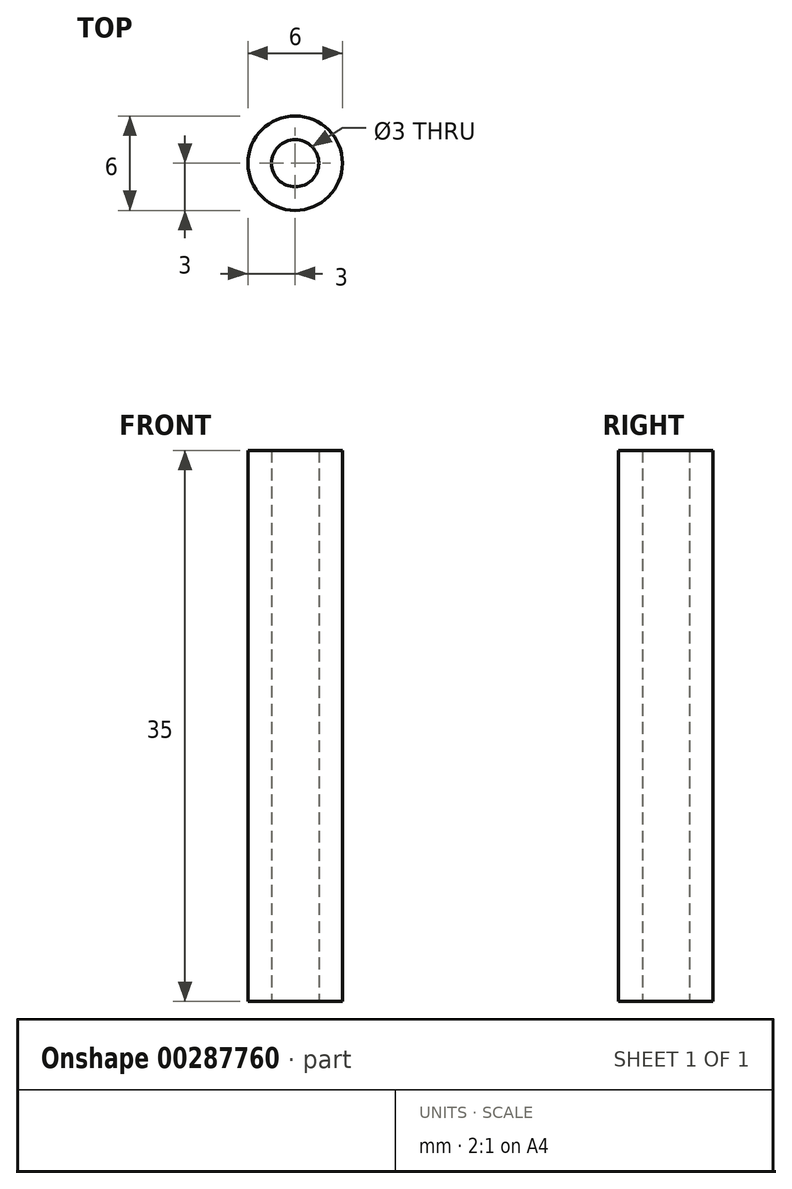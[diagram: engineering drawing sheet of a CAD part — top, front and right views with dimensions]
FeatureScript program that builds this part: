
annotation { "Feature Type Name" : "Feature", "Feature Type Description" : "" }
export const myFeature = defineFeature(function(context is Context, id is Id, definition is map)
    precondition{}
    {
        {
            var Q0;
            Q0=qCreatedBy(makeId("Top.planeOp"),FACE);
            var sketch = newSketch(context, id + "F0", { "sketchPlane" : qUnion([Q0])});
            skCircle(sketch, "E0", {"center": v(0, 0) * mm, "radius": 1.5 * mm});
            skCircle(sketch, "E1", {"center": v(0, 0) * mm, "radius": 3 * mm});
            skSolve(sketch);
        }
        {
            var Q0;
            Q0=qSketchRegion(id+"F0",true);
            extrude(context, id + "F1", {"entities" : qUnion([Q0]), "depth" : 35 * mm});
        }
    });
